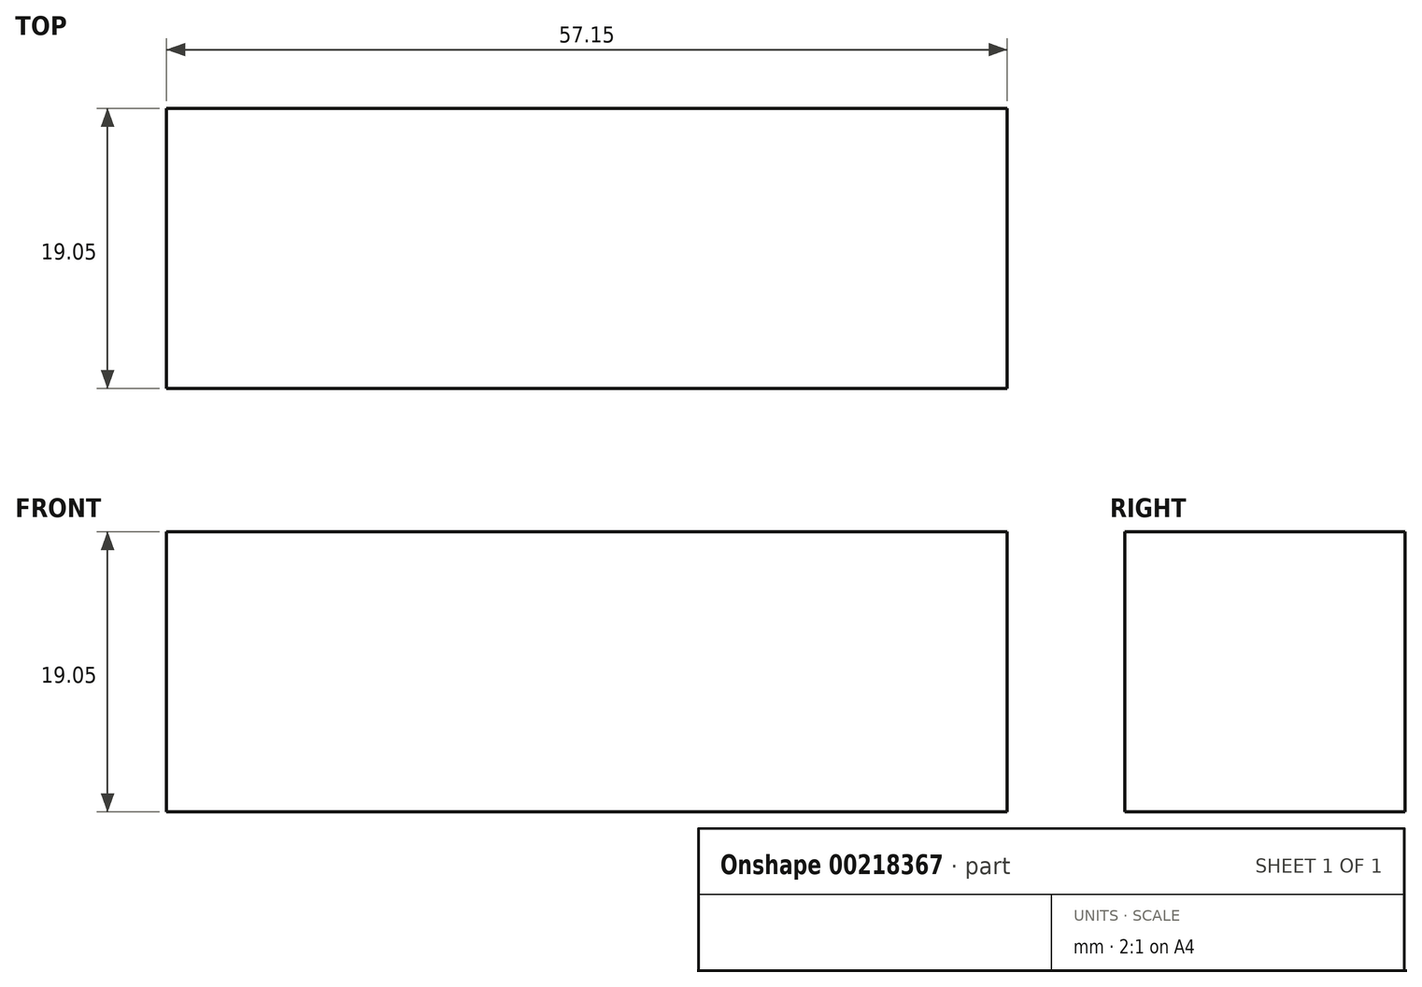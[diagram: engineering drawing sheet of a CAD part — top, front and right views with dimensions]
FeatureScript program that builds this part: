
annotation { "Feature Type Name" : "Feature", "Feature Type Description" : "" }
export const myFeature = defineFeature(function(context is Context, id is Id, definition is map)
    precondition{}
    {
        {
            var Q0;
            Q0=qCreatedBy(makeId("Front.planeOp"),FACE);
            var sketch = newSketch(context, id + "F0", { "sketchPlane" : qUnion([Q0])});
            skLineSegment(sketch, "E0.bottom", {"start": v(-33.45, 35.83) * mm, "end": v(-14.4, 35.83) * mm});
            skLineSegment(sketch, "E0.top", {"start": v(-33.45, 16.78) * mm, "end": v(-14.4, 16.78) * mm});
            skLineSegment(sketch, "E0.left", {"start": v(-33.45, 35.83) * mm, "end": v(-33.45, 16.78) * mm});
            skLineSegment(sketch, "E0.right", {"start": v(-14.4, 35.83) * mm, "end": v(-14.4, 16.78) * mm});
            skLineSegment(sketch, "E1.bottom", {"start": v(-14.4, 35.83) * mm, "end": v(4.65, 35.83) * mm});
            skLineSegment(sketch, "E1.top", {"start": v(-14.4, 16.78) * mm, "end": v(4.65, 16.78) * mm});
            skLineSegment(sketch, "E1.right", {"start": v(4.65, 35.83) * mm, "end": v(4.65, 16.78) * mm});
            skLineSegment(sketch, "E2.bottom", {"start": v(4.65, 35.83) * mm, "end": v(23.7, 35.83) * mm});
            skLineSegment(sketch, "E2.top", {"start": v(4.65, 16.78) * mm, "end": v(23.7, 16.78) * mm});
            skLineSegment(sketch, "E2.right", {"start": v(23.7, 35.83) * mm, "end": v(23.7, 16.78) * mm});
            skLineSegment(sketch, "E3.top", {"start": v(-14.4, 54.88) * mm, "end": v(4.65, 54.88) * mm});
            skLineSegment(sketch, "E3.left", {"start": v(-14.4, 35.83) * mm, "end": v(-14.4, 54.88) * mm});
            skLineSegment(sketch, "E3.right", {"start": v(4.65, 35.83) * mm, "end": v(4.65, 54.88) * mm});
            skSolve(sketch);
        }
        {
            var Q0;
            Q0=makeQuery(id+"F0.imprint","IMPRINT",FACE,{"disambiguationData":[TD([[makeQuery(id+"F0.imprint","IMPRINT",EDGE,{"derivedFrom":sQuery(id+"F0.wireOp",EDGE,"E0.bottom")}),-1.0]])]});
            var Q1;
            Q1=makeQuery(id+"F0.imprint","IMPRINT",FACE,{"disambiguationData":[TD([[makeQuery(id+"F0.imprint","IMPRINT",EDGE,{"derivedFrom":sQuery(id+"F0.wireOp",EDGE,"E1.top")}),1.0]])]});
            var Q2;
            Q2=makeQuery(id+"F0.imprint","IMPRINT",FACE,{"disambiguationData":[TD([[makeQuery(id+"F0.imprint","IMPRINT",EDGE,{"derivedFrom":sQuery(id+"F0.wireOp",EDGE,"E1.bottom")}),1.0]])]});
            var Q3;
            Q3=makeQuery(id+"F0.imprint","IMPRINT",FACE,{"disambiguationData":[TD([[makeQuery(id+"F0.imprint","IMPRINT",EDGE,{"derivedFrom":sQuery(id+"F0.wireOp",EDGE,"E2.bottom")}),-1.0]])]});
            extrude(context, id + "F1", {"entities" : qUnion([Q0, Q1, Q2, Q3]), "depth" : 19.05 * mm});
        }
    });
